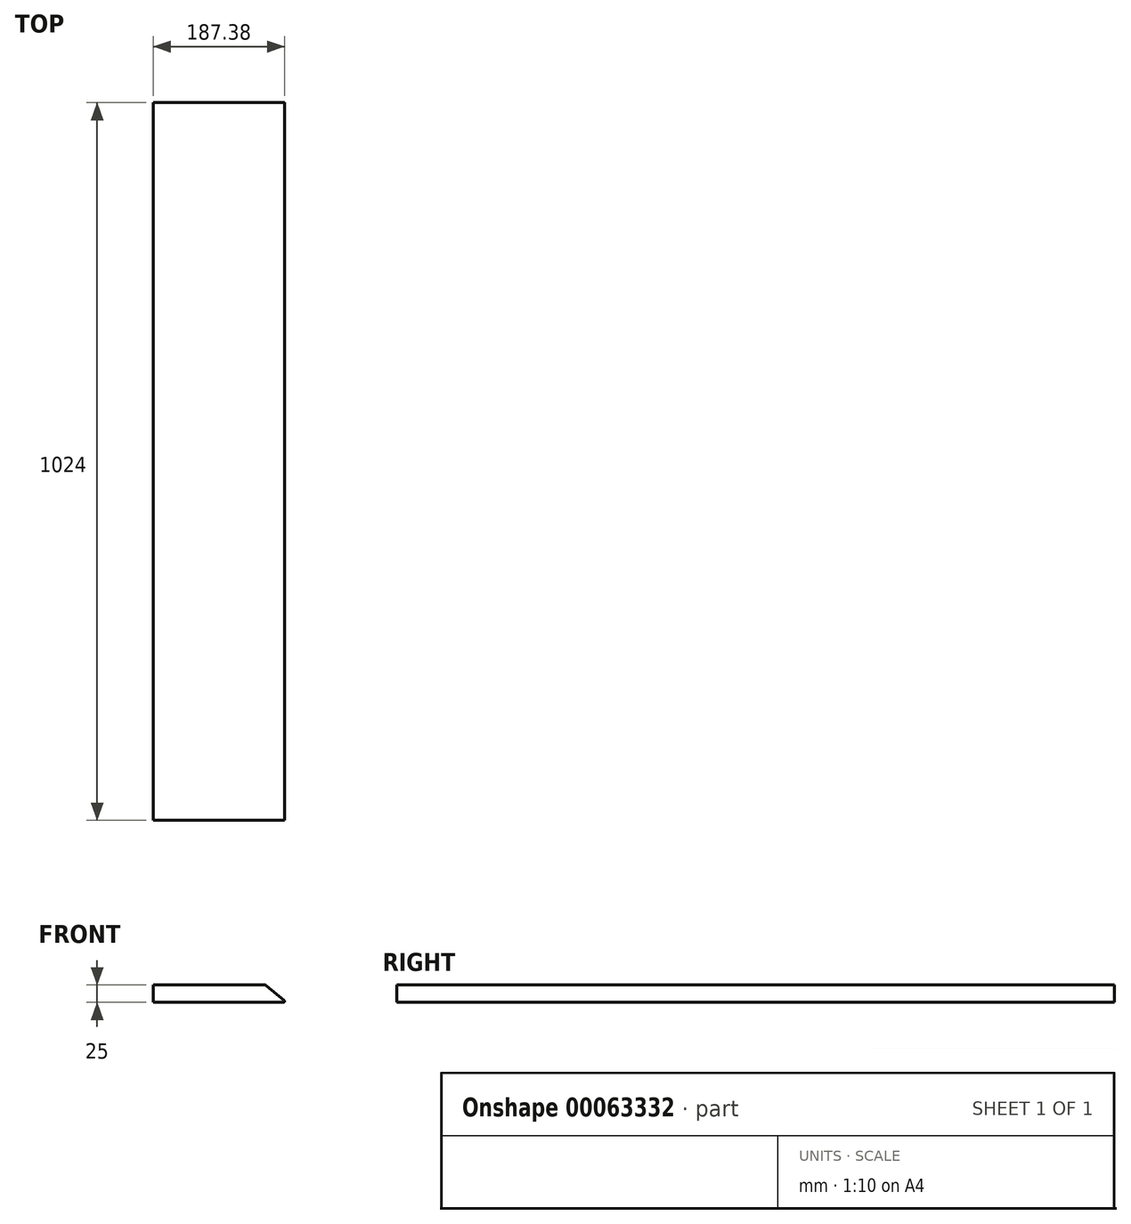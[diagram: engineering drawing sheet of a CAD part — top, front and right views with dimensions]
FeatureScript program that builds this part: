
annotation { "Feature Type Name" : "Feature", "Feature Type Description" : "" }
export const myFeature = defineFeature(function(context is Context, id is Id, definition is map)
    precondition{}
    {
        {
            var Q0;
            Q0=qCreatedBy(makeId("Top.planeOp"),FACE);
            var sketch = newSketch(context, id + "F0", { "sketchPlane" : qUnion([Q0])});
            skLineSegment(sketch, "E0.rect.bottom", {"start": v(95, 512) * mm, "end": v(-95, 512) * mm});
            skLineSegment(sketch, "E0.rect.top", {"start": v(95, -512) * mm, "end": v(-95, -512) * mm});
            skLineSegment(sketch, "E0.rect.left", {"start": v(95, 512) * mm, "end": v(95, -512) * mm});
            skLineSegment(sketch, "E0.rect.right", {"start": v(-95, 512) * mm, "end": v(-95, -512) * mm});
            skPoint(sketch, "E0.rect.middle", {"position": v(0, 0) * mm});
            skSolve(sketch);
        }
        {
            var Q0;
            Q0=makeQuery(id+"F0.imprint","IMPRINT",FACE,{"disambiguationData":[TD([[makeQuery(id+"F0.imprint","IMPRINT",EDGE,{"derivedFrom":sQuery(id+"F0.wireOp",EDGE,"E0.rect.bottom")}),1.0]])]});
            extrude(context, id + "F1", {"entities" : qUnion([Q0]), "depth" : 25 * mm});
        }
        {
            var Q0;
            Q0=makeQuery(id+"F1.opExtrude","SWEPT_FACE",FACE,{"disambiguationData":[OSD([sQuery(id+"F0.wireOp",EDGE,"E0.rect.top")])]});
            var sketch = newSketch(context, id + "F2", { "sketchPlane" : qUnion([Q0])});
            skLineSegment(sketch, "E1", {"start": v(66.6, 23.83) * mm, "end": v(91.84, 2.65) * mm});
            skLineSegment(sketch, "E2", {"start": v(65.2, 25) * mm, "end": v(95, 25) * mm});
            skLineSegment(sketch, "E3", {"start": v(95, 25) * mm, "end": v(95, 0) * mm});
            skLineSegment(sketch, "E4", {"start": v(-95, 25) * mm, "end": v(63.39, 25) * mm});
            skPoint(sketch, "E5.visualSharp", {"position": v(65.2, 25) * mm});
            skArc(sketch, "E5.filletArc", {"start": v(66.6, 23.83) * mm, "mid": v(65.1, 24.7) * mm, "end": v(63.39, 25) * mm});
            skLineSegment(sketch, "E6", {"start": v(-95, 0) * mm, "end": v(90.88, 0) * mm});
            skPoint(sketch, "E7.visualSharp", {"position": v(95, 0) * mm});
            skArc(sketch, "E7.filletArc", {"start": v(90.88, 0) * mm, "mid": v(92.29, 0.99) * mm, "end": v(91.84, 2.65) * mm});
            skSolve(sketch);
        }
        {
            var Q0;
            Q0=makeQuery(id+"F2.imprint","IMPRINT",FACE,{"disambiguationData":[TD([[makeQuery(id+"F2.imprint","IMPRINT",EDGE,{"derivedFrom":sQuery(id+"F2.wireOp",EDGE,"E1")}),1.0]])]});
            extrude(context, id + "F3", {"entities" : qUnion([Q0]), "operationType" : NewBodyOperationType.REMOVE, "oppositeDirection" : true, "depth" : 1024 * mm});
        }
    });
